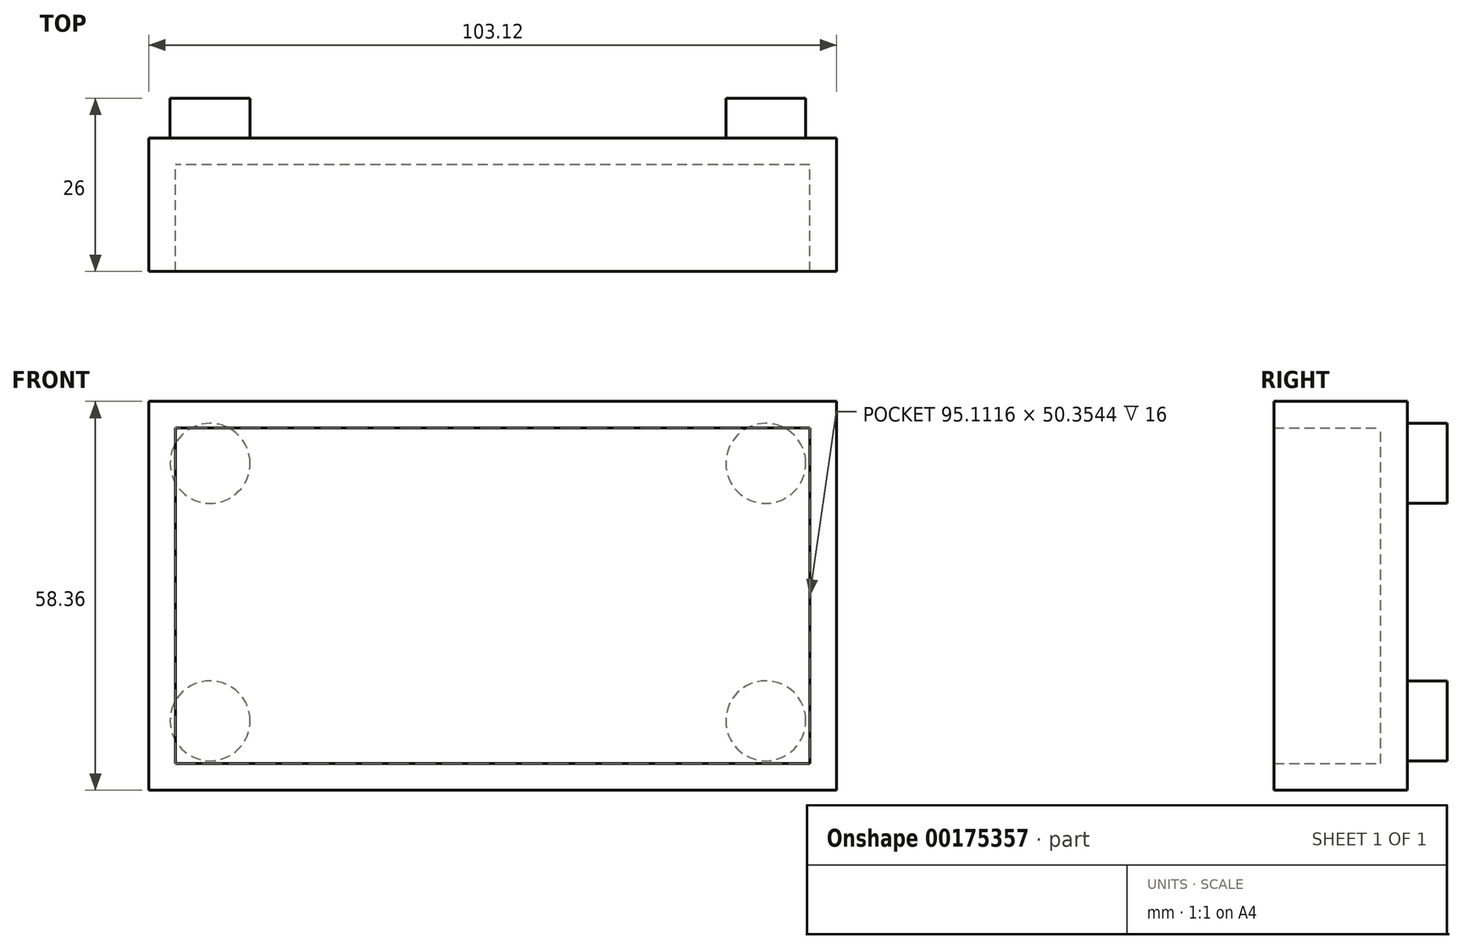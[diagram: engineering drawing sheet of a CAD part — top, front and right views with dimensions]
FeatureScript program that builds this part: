
annotation { "Feature Type Name" : "Feature", "Feature Type Description" : "" }
export const myFeature = defineFeature(function(context is Context, id is Id, definition is map)
    precondition{}
    {
        {
            var Q0;
            Q0=qCreatedBy(makeId("Front.planeOp"),FACE);
            var sketch = newSketch(context, id + "F0", { "sketchPlane" : qUnion([Q0])});
            skLineSegment(sketch, "E0.bottom", {"start": v(51.56, -29.18) * mm, "end": v(-51.56, -29.18) * mm});
            skLineSegment(sketch, "E0.top", {"start": v(51.56, 29.18) * mm, "end": v(-51.56, 29.18) * mm});
            skLineSegment(sketch, "E0.left", {"start": v(51.56, -29.18) * mm, "end": v(51.56, 29.18) * mm});
            skLineSegment(sketch, "E0.right", {"start": v(-51.56, -29.18) * mm, "end": v(-51.56, 29.18) * mm});
            skPoint(sketch, "E0.middle", {"position": v(0, 0) * mm});
            skSolve(sketch);
        }
        {
            var Q0;
            Q0 = qSketchRegion(id + "F0", true);
            extrude(context, id + "F1", {"entities" : qUnion([Q0]), "depth" : 20 * mm});
        }
        {
            var Q0;
            Q0=makeQuery(id+"F1.opExtrude","CAP_FACE",FACE,{"disambiguationData":[OSD([sQuery(id+"F0.wireOp",EDGE,"E0.bottom"),sQuery(id+"F0.wireOp",EDGE,"E0.top"),sQuery(id+"F0.wireOp",EDGE,"E0.left"),sQuery(id+"F0.wireOp",EDGE,"E0.right")])],"isStart":false});
            shell(context, id + "F2", {"entities" : qUnion([Q0]), "thickness" : 4 * mm});
        }
        {
            var Q0;
            Q0=qCreatedBy(makeId("Front.planeOp"),FACE);
            var sketch = newSketch(context, id + "F3", { "sketchPlane" : qUnion([Q0])});
            skCircle(sketch, "E1", {"center": v(-42.37, -18.75) * mm, "radius": 6 * mm});
            skCircle(sketch, "E2", {"center": v(40.96, -18.75) * mm, "radius": 6 * mm});
            skCircle(sketch, "E3", {"center": v(40.96, 19.89) * mm, "radius": 6 * mm});
            skCircle(sketch, "E4", {"center": v(-42.37, 19.89) * mm, "radius": 6 * mm});
            skSolve(sketch);
        }
        {
            var Q0;
            Q0 = qSketchRegion(id + "F3", true);
            extrude(context, id + "F4", {"entities" : qUnion([Q0]), "operationType" : NewBodyOperationType.ADD, "oppositeDirection" : true, "depth" : 6 * mm});
        }
    });
